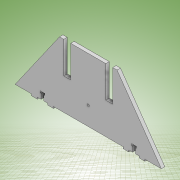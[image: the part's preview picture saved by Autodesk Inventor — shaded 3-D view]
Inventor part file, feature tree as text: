
AUTODESK INVENTOR PART (.ipt)
format: ipt  version: 2022 (Build 260153000, 153)  size: 197,120 bytes
history: native  units: mm
features: extrude x4, sketch x3, other x1
ambient origin geometry x8: Origin, YZ Plane, XZ Plane, XY Plane, X Axis, Y Axis, Z Axis, Center Point
bodies: Body1 (feature_tree)
feature tree (8):
  other  "Sólido1"
  extrude  "Extrusión1"  Depth=110.0mm
  extrude  "Extrusión3"  Depth=12.0mm
  extrude  "Extrusión4"  Depth=3.0mm
  extrude  "Extrusión5"  Depth=55.0mm
  sketch  "Boceto3"  dims[d1=100.0mm d2=110.0mm]
  sketch  "Boceto4"  dims[d3=61.0mm d5=12.0mm]
  sketch  "Boceto5"  dims[d6=7.5mm d7=9.599311mm d9=9.599311mm d12=55.0mm d13=6.0mm d14=0.0mm d23=9.599311mm d24=9.599311mm d25=5.0mm d26=8.0mm d27=12.0mm d29=45.0mm d30=3.0mm d31=3.0mm d32=0.0mm d33=10.0mm d34=18.0mm d35=10.0mm d36=3.0mm d37=0.0mm d39=4.0mm d40=32.0mm d41=0.0mm d42=0.0mm]
